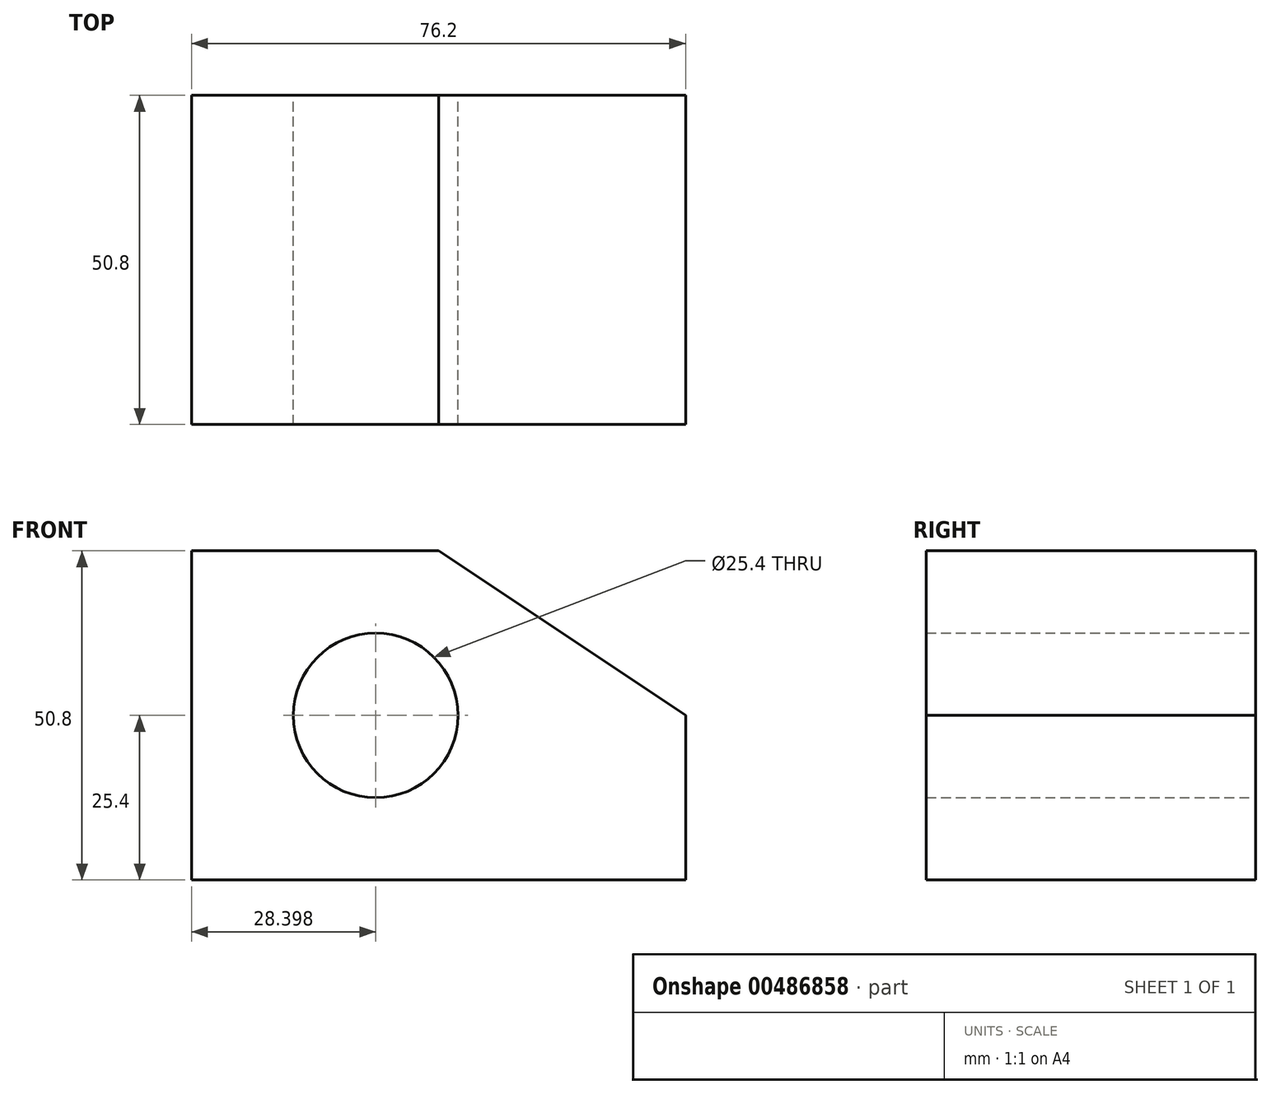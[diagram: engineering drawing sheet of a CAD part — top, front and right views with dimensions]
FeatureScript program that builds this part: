
annotation { "Feature Type Name" : "Feature", "Feature Type Description" : "" }
export const myFeature = defineFeature(function(context is Context, id is Id, definition is map)
    precondition{}
    {
        {
            var Q0;
            Q0=qCreatedBy(makeId("Front.planeOp"),FACE);
            var sketch = newSketch(context, id + "F0", { "sketchPlane" : qUnion([Q0])});
            skLineSegment(sketch, "E0.bottom", {"start": v(0, 25.4) * mm, "end": v(-38.1, 25.4) * mm});
            skLineSegment(sketch, "E0.top", {"start": v(38.1, -25.4) * mm, "end": v(-38.1, -25.4) * mm});
            skLineSegment(sketch, "E0.left", {"start": v(38.1, 0) * mm, "end": v(38.1, -25.4) * mm});
            skLineSegment(sketch, "E0.right", {"start": v(-38.1, 25.4) * mm, "end": v(-38.1, -25.4) * mm});
            skPoint(sketch, "E0.middle", {"position": v(0, 0) * mm});
            skLineSegment(sketch, "E1", {"start": v(0, 25.4) * mm, "end": v(38.1, 0) * mm});
            skPoint(sketch, "E2.orphan", {"position": v(38.1, 25.4) * mm});
            skCircle(sketch, "E3", {"center": v(-9.7, 0) * mm, "radius": 12.7 * mm});
            skSolve(sketch);
        }
        {
            var Q0;
            Q0 = qSketchRegion(id + "F0", true);
            extrude(context, id + "F1", {"entities" : qUnion([Q0]), "depth" : 50.8 * mm});
        }
    });
